# Revit family: 130401-00001
name_source: partatom
category: Обобщенные модели
units: mm (PartAtom-declared; Revit-internal decimal feet)

## family parameters
Всегда вертикально = Да
Может служить основой для арматурных стержней = Нет
На основе рабочей плоскости = Нет
Общий = Нет
При загрузке вырезать с полостями = Нет
Размер круглого соединителя = Использовать диаметр
Тип детали = Нормальный
Точка расчета площади = Нет

## types (1)
- Кросс ШКОН -Р/1 -4 -FC/ST  -(корпус)
    ADSK_Высота = 131 мм
    ADSK_Декларация о соответствии = https://www.ssd.ru
    ADSK_Длина = 115 мм
    ADSK_Изготовитель = АО "СВЯЗЬСТРОЙДЕТАЛЬ"
    ADSK_Код изделия = 130401-00001
    ADSK_Макс. диаметр ОК, мм = 15
    ADSK_Макс. кол-во вводимых ОК = 1
    ADSK_Марка = Настенные оптические кроссы ШКОН-Р
    ADSK_Масса, кг = 0,33
    ADSK_Материал корпуса = Сталь
    ADSK_Наименование = Кросс ШКОН -Р/1 -4 -FC/ST ~ -(корпус) ~
    ADSK_Ссылка на сайт = https://www.ssd.ru
    ADSK_Ширина = 26 мм
    Отметка по умолчанию = 0 мм
